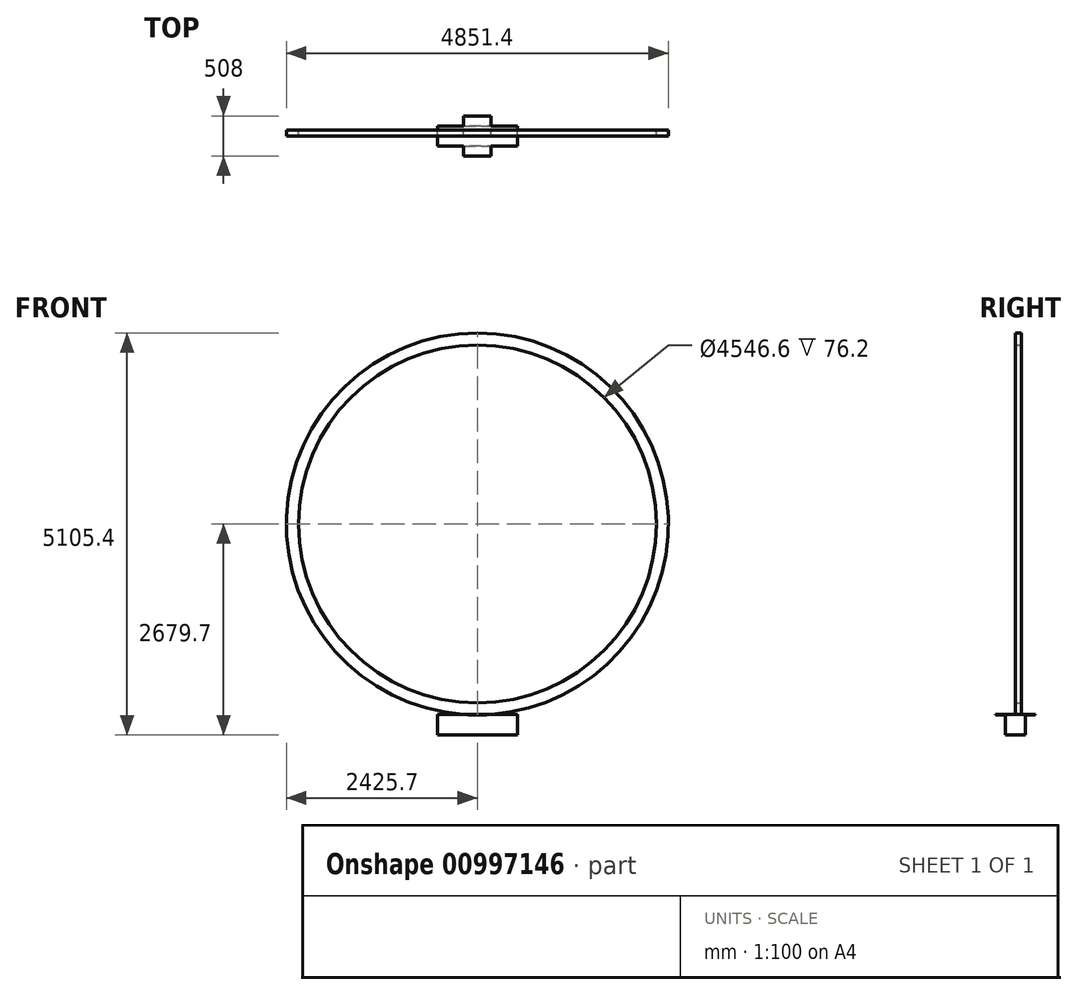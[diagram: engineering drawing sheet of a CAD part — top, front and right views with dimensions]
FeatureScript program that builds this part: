
annotation { "Feature Type Name" : "Feature", "Feature Type Description" : "" }
export const myFeature = defineFeature(function(context is Context, id is Id, definition is map)
    precondition{}
    {
        {
            var Q0;
            Q0=qCreatedBy(makeId("Front.planeOp"),FACE);
            var sketch = newSketch(context, id + "F0", { "sketchPlane" : qUnion([Q0])});
            skCircle(sketch, "E0", {"center": v(0, 0) * mm, "radius": 2273.3 * mm});
            skCircle(sketch, "E1.0", {"center": v(0, 0) * mm, "radius": 2425.7 * mm});
            skSolve(sketch);
        }
        {
            var Q0;
            Q0=makeQuery(id+"F0.imprint","IMPRINT",FACE,{"disambiguationData":[TD([[makeQuery(id+"F0.imprint","IMPRINT",EDGE,{"derivedFrom":sQuery(id+"F0.wireOp",EDGE,"E0")}),-1.0]])]});
            extrude(context, id + "F1", {"entities" : qUnion([Q0]), "depth" : 76.2 * mm, "offsetDistance" : 25.4 * mm});
        }
        {
            var Q0;
            Q0=makeQuery(id+"F1.opExtrude","CAP_FACE",FACE,{"disambiguationData":[OSD([sQuery(id+"F0.wireOp",EDGE,"E0"),sQuery(id+"F0.wireOp",EDGE,"E1.0")])],"isStart":false});
            var sketch = newSketch(context, id + "F2", { "sketchPlane" : qUnion([Q0])});
            skLineSegment(sketch, "E2.bottom", {"start": v(0, -2419.35) * mm, "end": v(508, -2419.35) * mm});
            skLineSegment(sketch, "E2.top", {"start": v(0, -2679.7) * mm, "end": v(508, -2679.7) * mm});
            skLineSegment(sketch, "E2.right", {"start": v(508, -2419.35) * mm, "end": v(508, -2679.7) * mm});
            skLineSegment(sketch, "E3.bottom", {"start": v(0, -2419.35) * mm, "end": v(-508, -2419.35) * mm});
            skLineSegment(sketch, "E3.top", {"start": v(0, -2679.7) * mm, "end": v(-508, -2679.7) * mm});
            skLineSegment(sketch, "E3.right", {"start": v(-508, -2419.35) * mm, "end": v(-508, -2679.7) * mm});
            skSolve(sketch);
        }
        {
            var Q0;
            Q0=makeQuery(id+"F2.imprint","IMPRINT",FACE,{"disambiguationData":[TD([[makeQuery(id+"F2.imprint","IMPRINT",EDGE,{"derivedFrom":sQuery(id+"F2.wireOp",EDGE,"E2.top")}),1.0]])]});
            extrude(context, id + "F3", {"entities" : qUnion([Q0]), "operationType" : NewBodyOperationType.ADD, "endBound" : BoundingType.SYMMETRIC, "depth" : 254 * mm, "offsetDistance" : 25.4 * mm});
        }
        {
            var Q0;
            Q0=makeQuery(id+"F2.imprint","IMPRINT",FACE,{"disambiguationData":[TD([[makeQuery(id+"F2.imprint","IMPRINT",EDGE,{"derivedFrom":sQuery(id+"F2.wireOp",EDGE,"E2.bottom")}),-1.0]])]});
            extrude(context, id + "F4", {"entities" : qUnion([Q0]), "operationType" : NewBodyOperationType.ADD, "endBound" : BoundingType.SYMMETRIC, "depth" : 508 * mm, "offsetDistance" : 25.4 * mm});
        }
    });
